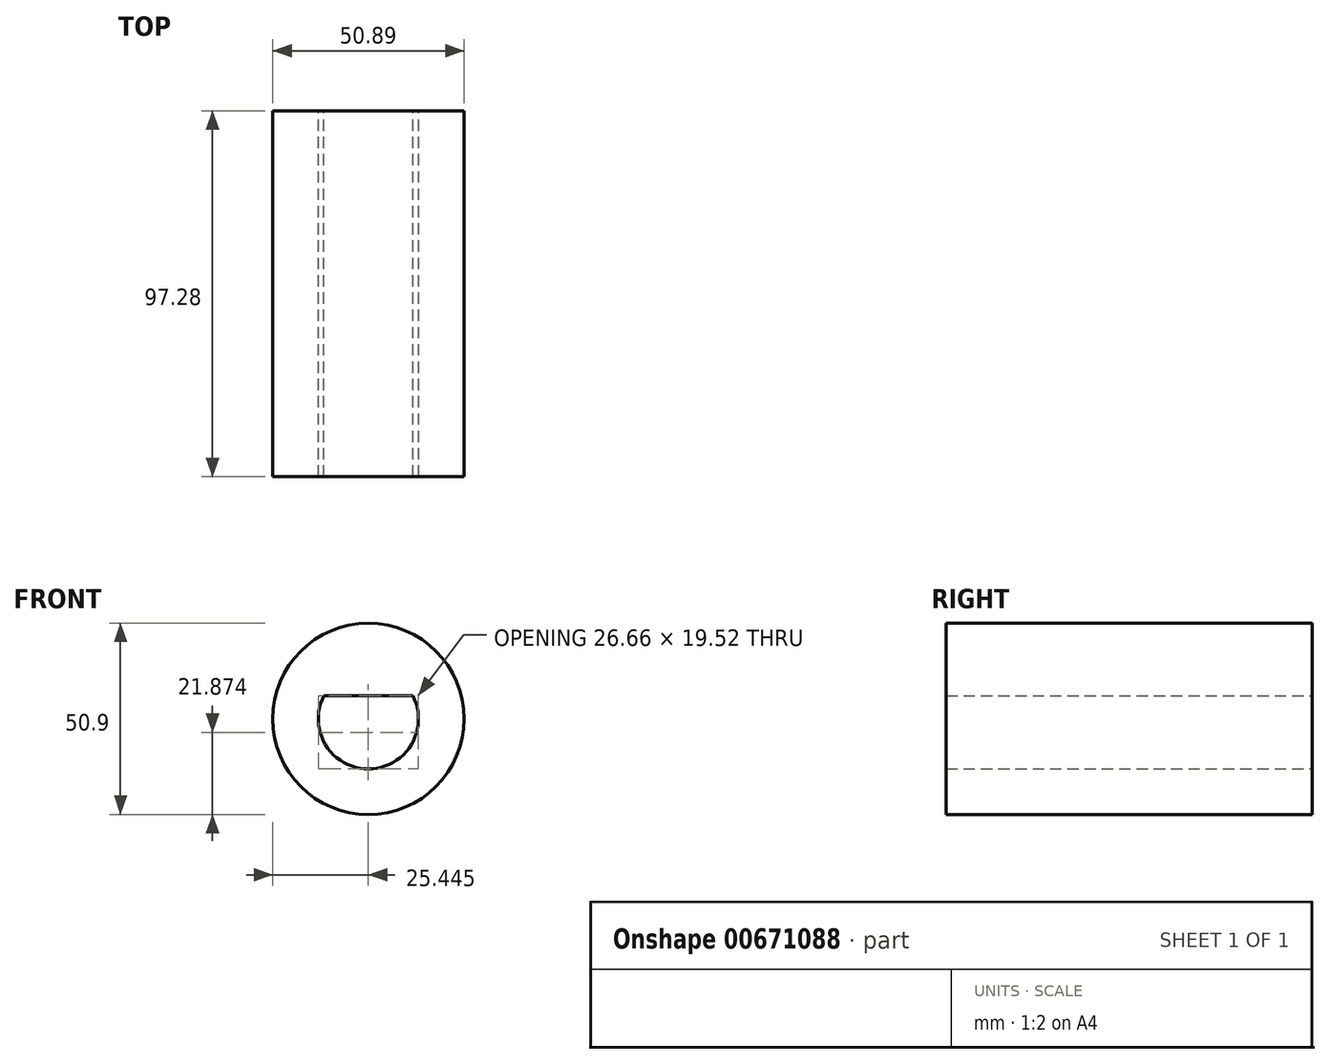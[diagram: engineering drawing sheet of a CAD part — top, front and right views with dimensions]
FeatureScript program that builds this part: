
annotation { "Feature Type Name" : "Feature", "Feature Type Description" : "" }
export const myFeature = defineFeature(function(context is Context, id is Id, definition is map)
    precondition{}
    {
        {
            var Q0;
            Q0=qCreatedBy(makeId("Front.planeOp"),FACE);
            var sketch = newSketch(context, id + "F0", { "sketchPlane" : qUnion([Q0])});
            skCircle(sketch, "E0", {"center": v(-37.81, 24.96) * mm, "radius": 25.45 * mm});
            skCircle(sketch, "E1", {"center": v(-37.81, 24.96) * mm, "radius": 13.34 * mm});
            skLineSegment(sketch, "E2", {"start": v(-49.63, 31.14) * mm, "end": v(-26, 31.14) * mm});
            skSolve(sketch);
        }
        {
            var Q0;
            Q0=makeQuery(id+"F0.imprint","IMPRINT",FACE,{"disambiguationData":[TD([[makeQuery(id+"F0.imprint","IMPRINT",EDGE,{"derivedFrom":sQuery(id+"F0.wireOp",EDGE,"E0")}),1.0]])]});
            var Q1;
            {var subQ0=sQuery(id+"F0.wireOp",EDGE,"E2");Q1=makeQuery(id+"F0.imprint","IMPRINT",FACE,{"disambiguationData":[TD([[makeQuery(id+"F0.imprint","IMPRINT",EDGE,{"derivedFrom":subQ0}),1.0]])]});}
            extrude(context, id + "F1", {"entities" : qUnion([Q0, Q1]), "depth" : 97.28 * mm, "offsetDistance" : 25.4 * mm});
        }
    });
